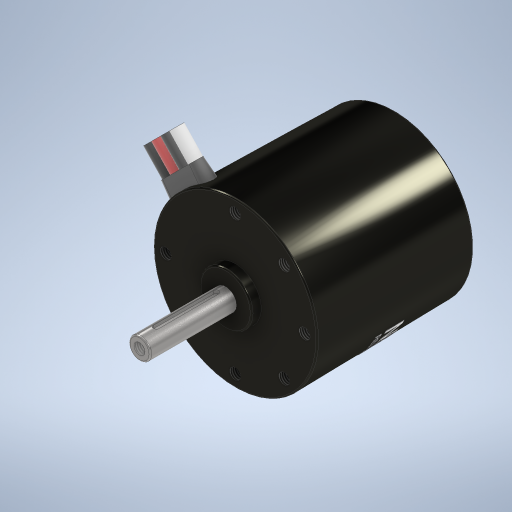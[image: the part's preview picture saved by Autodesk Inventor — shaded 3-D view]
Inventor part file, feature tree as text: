
AUTODESK INVENTOR PART (.ipt)
format: ipt  version: 2024.2 (Build 282272000, 272)  size: 3,570,688 bytes
history: native  units: in
note: dims shown in document units (in); Inventor stores cm internally (conversion verified against a paired STEP export)
features: thread x9, other x1
ambient origin geometry x8: Origin, YZ Plane, XZ Plane, XY Plane, X Axis, Y Axis, Z Axis, Center Point
bodies: Solid1 (feature_tree)
feature tree (10):
  thread  "Thread1"  [1 undecoded]
  thread  "Thread2"  [1 undecoded]
  thread  "Thread3"  [1 undecoded]
  thread  "Thread4"  [1 undecoded]
  thread  "Thread5"  [1 undecoded]
  thread  "Thread6"  [1 undecoded]
  thread  "Thread7"  [1 undecoded]
  thread  "Thread8"  [1 undecoded]
  thread  "Thread9"  [1 undecoded]
  other  "Wrap2"
note: 9 required parameter values undecoded (feature->parameter linkage not recoverable at this tier; creation-order binding heuristic only, values carry confidence <= 0.55)
